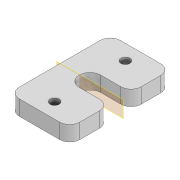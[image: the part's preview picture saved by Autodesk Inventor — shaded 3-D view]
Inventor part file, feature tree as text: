
AUTODESK INVENTOR PART (.ipt)
format: ipt  version: 2020 (Build 240168000, 168)  size: 130,048 bytes
history: native  units: mm
features: extrude x4, sketch x4, mirror x2, plane x1, fillet x1
ambient origin geometry x8: Origin, YZ Plane, XZ Plane, XY Plane, X Axis, Y Axis, Z Axis, Center Point
bodies: Solid1 (feature_tree)
feature tree (12):
  extrude  "Extrusion1"  Depth=40.0mm
  extrude  "Extrusion2"  Depth=8.5mm
  extrude  "Extrusion3"  Depth=6.0mm
  plane  "Work Plane1"
  mirror  "Mirror1"
  extrude  "Extrusion4"  [1 undecoded]
  mirror  "Mirror2"
  fillet  "Fillet1"  Radius=5.8mm
  sketch  "Sketch1"  dims[d0=24.0mm d1=40.0mm]
  sketch  "Sketch2"  dims[d2=6.0mm d3=0.0mm d4=8.5mm]
  sketch  "Sketch3"  dims[d5=6.0mm d6=0.0mm d7=3.6mm]
  sketch  "Sketch4"  dims[d8=6.0mm d9=0.0mm d10=-20.0mm d11=5.8mm d12=3.0mm d13=0.0mm d14=4.0mm]
note: 1 required parameter value undecoded (feature->parameter linkage not recoverable at this tier; creation-order binding heuristic only, values carry confidence <= 0.55)
